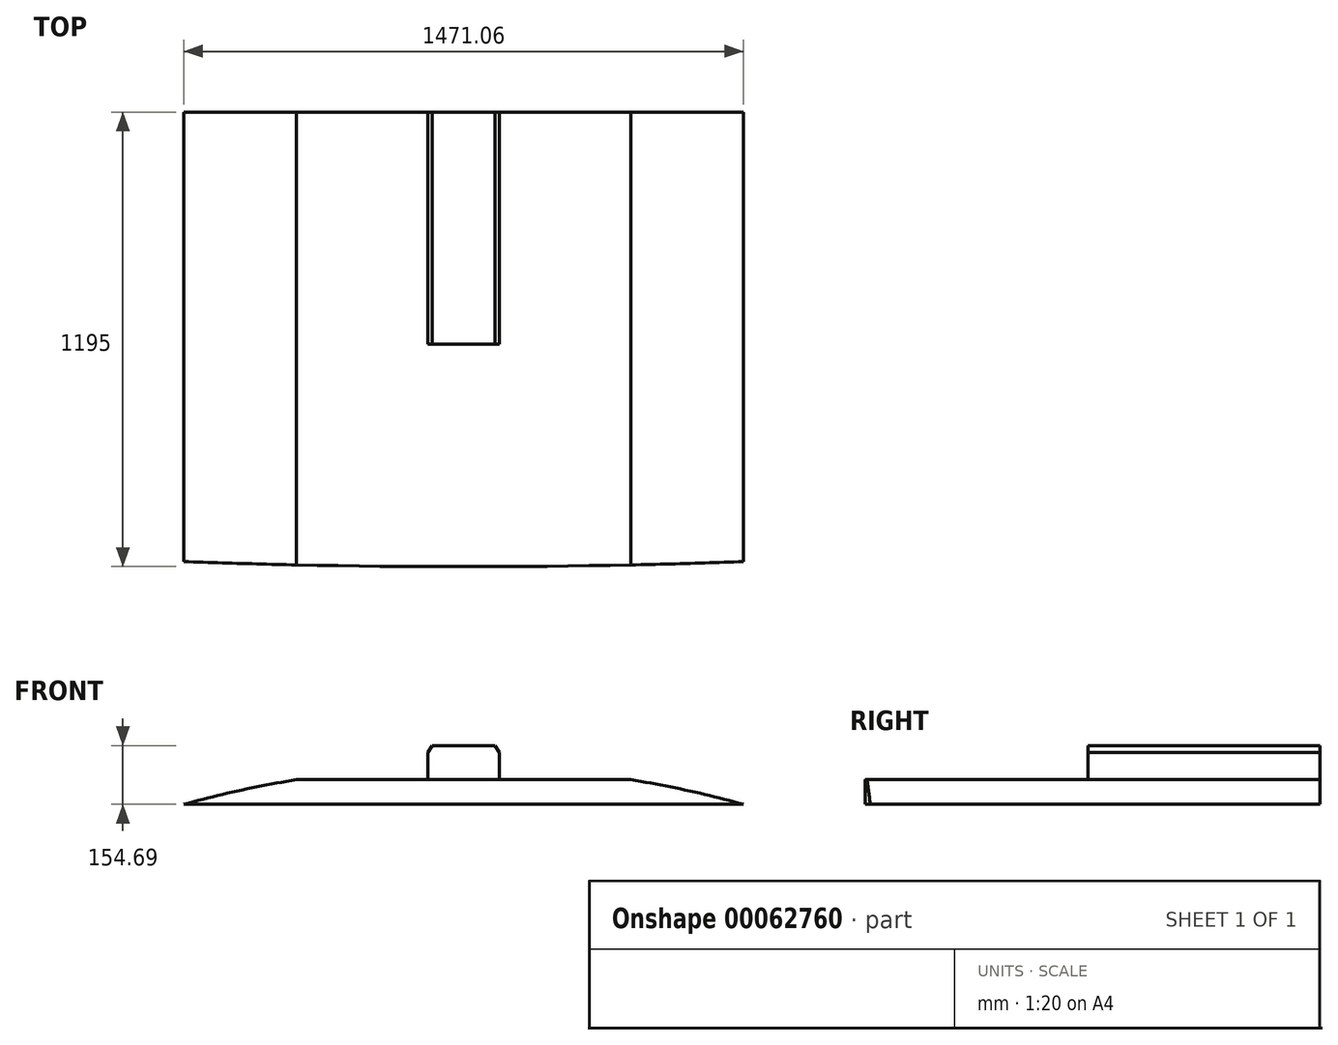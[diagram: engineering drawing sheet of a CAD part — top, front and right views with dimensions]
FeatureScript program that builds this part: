
annotation { "Feature Type Name" : "Feature", "Feature Type Description" : "" }
export const myFeature = defineFeature(function(context is Context, id is Id, definition is map)
    precondition{}
    {
        {
            var Q0;
            Q0=qCreatedBy(makeId("Front.planeOp"),FACE);
            var sketch = newSketch(context, id + "F0", { "sketchPlane" : qUnion([Q0])});
            skArc(sketch, "E0", {"start": v(1235.52, 2462.42) * mm, "mid": v(634.84, 2680.86) * mm, "end": v(0, 2755) * mm});
            skLineSegment(sketch, "E1", {"start": v(0, 0) * mm, "end": v(1355.2, 0) * mm, "construction": true});
            skLineSegment(sketch, "E2", {"start": v(1355.2, 0) * mm, "end": v(1355.2, 2268.47) * mm, "construction": true});
            skArc(sketch, "E3", {"start": v(1355.2, 2268.47) * mm, "mid": v(1322.87, 2382.42) * mm, "end": v(1235.52, 2462.42) * mm});
            skLineSegment(sketch, "E4", {"start": v(0, 0) * mm, "end": v(1407, 0) * mm, "construction": true});
            skLineSegment(sketch, "E5", {"start": v(1407, 0) * mm, "end": v(1407, 2368.62) * mm, "construction": true});
            skLineSegment(sketch, "E6", {"start": v(1355.2, 2268.47) * mm, "end": v(1357.8, 2155) * mm});
            skLineSegment(sketch, "E7", {"start": v(0, 2755) * mm, "end": v(0, 2155) * mm, "construction": true});
            skLineSegment(sketch, "E8", {"start": v(0, 2155) * mm, "end": v(1357.8, 2155) * mm});
            skArc(sketch, "E9.trimOffspring", {"start": v(1407, 2368.62) * mm, "mid": v(1381.18, 2383.77) * mm, "end": v(1355.2, 2398.64) * mm});
            skArc(sketch, "E10.MirrorCS", {"start": v(-1235.52, 2462.42) * mm, "mid": v(-634.84, 2680.86) * mm, "end": v(0, 2755) * mm});
            skArc(sketch, "E11.MirrorCS", {"start": v(-1355.2, 2268.47) * mm, "mid": v(-1322.87, 2382.42) * mm, "end": v(-1235.52, 2462.42) * mm});
            skLineSegment(sketch, "E12.MirrorCS", {"start": v(-1355.2, 2268.47) * mm, "end": v(-1357.8, 2155) * mm});
            skLineSegment(sketch, "E13.MirrorCS", {"start": v(0, 2155) * mm, "end": v(-1357.8, 2155) * mm});
            skSolve(sketch);
        }
        {
            var Q0;
            Q0=makeQuery(id+"F0.imprint","IMPRINT",FACE,{"disambiguationData":[TD([[makeQuery(id+"F0.imprint","IMPRINT",EDGE,{"derivedFrom":sQuery(id+"F0.wireOp",EDGE,"E0")}),1.0]])]});
            extrude(context, id + "F1", {"entities" : qUnion([Q0]), "oppositeDirection" : true, "depth" : 2000 * mm});
        }
        {
            var Q0;
            Q0=makeQuery(id+"F1.opExtrude","SWEPT_FACE",FACE,{"disambiguationData":[OSD([sQuery(id+"F0.wireOp",EDGE,"E8"),sQuery(id+"F0.wireOp",EDGE,"E13.MirrorCS")])]});
            var sketch = newSketch(context, id + "F2", { "sketchPlane" : qUnion([Q0])});
            skArc(sketch, "E14", {"start": v(1357.8, -50) * mm, "mid": v(0, -5) * mm, "end": v(-1357.8, -50) * mm});
            skLineSegment(sketch, "E15.0", {"start": v(1357.8, 0) * mm, "end": v(-1357.8, 0) * mm});
            skLineSegment(sketch, "E16", {"start": v(1357.8, -50) * mm, "end": v(1357.8, 0) * mm});
            skLineSegment(sketch, "E17", {"start": v(-1357.8, -50) * mm, "end": v(-1357.8, 0) * mm});
            skSolve(sketch);
        }
        {
            var Q0;
            Q0=qSketchRegion(id+"F2",true);
            extrude(context, id + "F3", {"entities" : qUnion([Q0]), "operationType" : NewBodyOperationType.REMOVE, "endBound" : BoundingType.THROUGH_ALL, "oppositeDirection" : true, "depth" : 25 * mm});
        }
        {
            var Q0;
            Q0=makeQuery(id+"F1.opExtrude","CAP_FACE",FACE,{"disambiguationData":[OSD([sQuery(id+"F0.wireOp",EDGE,"E0"),sQuery(id+"F0.wireOp",EDGE,"E3"),sQuery(id+"F0.wireOp",EDGE,"E6"),sQuery(id+"F0.wireOp",EDGE,"E8"),sQuery(id+"F0.wireOp",EDGE,"E10.MirrorCS"),sQuery(id+"F0.wireOp",EDGE,"E11.MirrorCS"),sQuery(id+"F0.wireOp",EDGE,"E12.MirrorCS"),sQuery(id+"F0.wireOp",EDGE,"E13.MirrorCS")])],"isStart":false});
            var sketch = newSketch(context, id + "F4", { "sketchPlane" : qUnion([Q0])});
            skPoint(sketch, "E18", {"position": v(0, 2755) * mm});
            skSolve(sketch);
        }
        {
            var Q0;
            Q0=makeQuery(id+"F4.imprint","IMPRINT",FACE,{"disambiguationData":[TD([[makeQuery(id+"F4.imprint","IMPRINT",EDGE,{"derivedFrom":makeQuery(id+"F1.opExtrude","CAP_EDGE",EDGE,{"disambiguationData":[OSD([sQuery(id+"F0.wireOp",EDGE,"E3")])],"isStart":false})}),-1.0]])]});
            var sketch = newSketch(context, id + "F5", { "sketchPlane" : qUnion([Q0])});
            skArc(sketch, "E19.0", {"start": v(-290, 2739.7) * mm, "mid": v(0, 2755) * mm, "end": v(290, 2739.7) * mm, "construction": true});
            skLineSegment(sketch, "E20", {"start": v(0, 2739.7) * mm, "end": v(290, 2739.7) * mm, "construction": true});
            skPoint(sketch, "E20.startSnap0", {"position": v(0, 2755) * mm});
            skLineSegment(sketch, "E21", {"start": v(0, 2739.7) * mm, "end": v(0, 2755) * mm, "construction": true});
            skLineSegment(sketch, "E22.MirrorCS", {"start": v(0, 2739.7) * mm, "end": v(-290, 2739.7) * mm, "construction": true});
            skPoint(sketch, "E23.orphan", {"position": v(1235.52, 2462.42) * mm});
            skPoint(sketch, "E24.orphan", {"position": v(-1235.52, 2462.42) * mm});
            skLineSegment(sketch, "E25", {"start": v(0, 2739.7) * mm, "end": v(0, 2719.7) * mm, "construction": true});
            skLineSegment(sketch, "E26", {"start": v(0, 2719.7) * mm, "end": v(439.65, 2719.7) * mm});
            skArc(sketch, "E27.0", {"start": v(0, 2755) * mm, "mid": v(634.84, 2680.86) * mm, "end": v(1235.52, 2462.42) * mm});
            skArc(sketch, "E28.MirrorCS", {"start": v(0, 2755) * mm, "mid": v(-634.84, 2680.86) * mm, "end": v(-1235.52, 2462.42) * mm});
            skLineSegment(sketch, "E29.MirrorCS", {"start": v(0, 2719.7) * mm, "end": v(-439.65, 2719.7) * mm});
            skSolve(sketch);
        }
        {
            var Q0;
            Q0=qSketchRegion(id+"F5",true);
            extrude(context, id + "F6", {"entities" : qUnion([Q0]), "operationType" : NewBodyOperationType.REMOVE, "endBound" : BoundingType.THROUGH_ALL, "oppositeDirection" : true, "depth" : 25 * mm});
        }
        {
            var Q0;
            Q0=makeQuery(id+"F4.imprint","IMPRINT",FACE,{"disambiguationData":[TD([[makeQuery(id+"F4.imprint","IMPRINT",EDGE,{"derivedFrom":makeQuery(id+"F1.opExtrude","CAP_EDGE",EDGE,{"disambiguationData":[OSD([sQuery(id+"F0.wireOp",EDGE,"E3")])],"isStart":false})}),-1.0]])]});
            var sketch = newSketch(context, id + "F7", { "sketchPlane" : qUnion([Q0])});
            skLineSegment(sketch, "E30.0", {"start": v(93.5, 2719.7) * mm, "end": v(-93.5, 2719.7) * mm});
            skLineSegment(sketch, "E31", {"start": v(0, 2719.7) * mm, "end": v(93.5, 2719.7) * mm, "construction": true});
            skLineSegment(sketch, "E32", {"start": v(93.5, 2719.7) * mm, "end": v(93.5, 2791.7) * mm});
            skLineSegment(sketch, "E33", {"start": v(93.5, 2791.7) * mm, "end": v(83.1, 2809.7) * mm});
            skLineSegment(sketch, "E34", {"start": v(83.1, 2809.7) * mm, "end": v(0, 2809.7) * mm});
            skLineSegment(sketch, "E35", {"start": v(0, 2809.7) * mm, "end": v(0, 2719.7) * mm, "construction": true});
            skLineSegment(sketch, "E36.MirrorCS", {"start": v(-83.1, 2809.7) * mm, "end": v(0, 2809.7) * mm});
            skLineSegment(sketch, "E37.MirrorCS", {"start": v(-93.5, 2791.7) * mm, "end": v(-83.1, 2809.7) * mm});
            skLineSegment(sketch, "E38.MirrorCS", {"start": v(-93.5, 2719.7) * mm, "end": v(-93.5, 2791.7) * mm});
            skSolve(sketch);
        }
        {
            var Q0;
            {var subQ5=sQuery(id+"F7.wireOp",EDGE,"E33");Q0=makeQuery(id+"F7.imprint","IMPRINT",FACE,{"disambiguationData":[TD([[makeQuery(id+"F7.imprint","IMPRINT",EDGE,{"derivedFrom":subQ5}),1.0]])]});}
            var Q1;
            {var subQ3=sQuery(id+"F7.wireOp",EDGE,"E30.0");Q1=makeQuery(id+"F7.imprint","IMPRINT",FACE,{"disambiguationData":[TD([[makeQuery(id+"F7.imprint","IMPRINT",EDGE,{"derivedFrom":subQ3}),-1.0]])]});}
            var Q2;
            {var subQ5=sQuery(id+"F7.wireOp",EDGE,"E31");Q2=makeQuery(id+"F7.imprint","IMPRINT",FACE,{"disambiguationData":[TD([[makeQuery(id+"F7.imprint","IMPRINT",EDGE,{"derivedFrom":subQ5}),1.0]])]});}
            var Q3;
            {var subQ3=sQuery(id+"F7.wireOp",EDGE,"E36.MirrorCS");Q3=makeQuery(id+"F7.imprint","IMPRINT",FACE,{"disambiguationData":[TD([[makeQuery(id+"F7.imprint","IMPRINT",EDGE,{"derivedFrom":subQ3}),-1.0]])]});}
            extrude(context, id + "F8", {"entities" : qUnion([Q0, Q1, Q2, Q3]), "operationType" : NewBodyOperationType.ADD, "oppositeDirection" : true, "depth" : (900 + 510) * mm});
        }
        {
            var Q0;
            Q0=makeQuery(id+"F4.imprint","IMPRINT",FACE,{"disambiguationData":[TD([[makeQuery(id+"F4.imprint","IMPRINT",EDGE,{"derivedFrom":makeQuery(id+"F1.opExtrude","CAP_EDGE",EDGE,{"disambiguationData":[OSD([sQuery(id+"F0.wireOp",EDGE,"E3")])],"isStart":false})}),-1.0]])]});
            var sketch = newSketch(context, id + "F9", { "sketchPlane" : qUnion([Q0])});
            skArc(sketch, "E39.0.0", {"start": v(1235.52, 2462.42) * mm, "mid": v(847.4, 2621.44) * mm, "end": v(439.65, 2719.7) * mm});
            skLineSegment(sketch, "E39.0.1", {"start": v(439.65, 2719.7) * mm, "end": v(93.5, 2719.7) * mm});
            skLineSegment(sketch, "E39.0.2", {"start": v(93.5, 2719.7) * mm, "end": v(93.5, 2791.7) * mm});
            skLineSegment(sketch, "E39.0.3", {"start": v(93.5, 2791.7) * mm, "end": v(83.1, 2809.7) * mm});
            skLineSegment(sketch, "E39.0.4", {"start": v(83.1, 2809.7) * mm, "end": v(-83.1, 2809.7) * mm});
            skLineSegment(sketch, "E39.0.5", {"start": v(-83.1, 2809.7) * mm, "end": v(-93.5, 2791.7) * mm});
            skLineSegment(sketch, "E39.0.6", {"start": v(-93.5, 2791.7) * mm, "end": v(-93.5, 2719.7) * mm});
            skLineSegment(sketch, "E39.0.7", {"start": v(-93.5, 2719.7) * mm, "end": v(-439.65, 2719.7) * mm});
            skArc(sketch, "E39.0.8", {"start": v(-439.65, 2719.7) * mm, "mid": v(-847.4, 2621.44) * mm, "end": v(-1235.52, 2462.42) * mm});
            skArc(sketch, "E39.0.9", {"start": v(-1235.52, 2462.42) * mm, "mid": v(-1322.87, 2382.42) * mm, "end": v(-1355.2, 2268.47) * mm});
            skLineSegment(sketch, "E39.0.10", {"start": v(-1355.2, 2268.47) * mm, "end": v(-1357.8, 2155) * mm});
            skLineSegment(sketch, "E39.0.11", {"start": v(-1357.8, 2155) * mm, "end": v(1357.8, 2155) * mm});
            skLineSegment(sketch, "E39.0.12", {"start": v(1357.8, 2155) * mm, "end": v(1355.2, 2268.47) * mm});
            skArc(sketch, "E39.0.13", {"start": v(1355.2, 2268.47) * mm, "mid": v(1322.87, 2382.42) * mm, "end": v(1235.52, 2462.42) * mm});
            skSolve(sketch);
        }
        {
            var Q0;
            Q0=qSketchRegion(id+"F9",true);
            extrude(context, id + "F10", {"entities" : qUnion([Q0]), "operationType" : NewBodyOperationType.REMOVE, "oppositeDirection" : true, "depth" : 800 * mm});
        }
        {
            var Q0;
            Q0=makeQuery(id+"F4.imprint","IMPRINT",FACE,{"disambiguationData":[TD([[makeQuery(id+"F4.imprint","IMPRINT",EDGE,{"derivedFrom":makeQuery(id+"F1.opExtrude","CAP_EDGE",EDGE,{"disambiguationData":[OSD([sQuery(id+"F0.wireOp",EDGE,"E3")])],"isStart":false})}),-1.0]])]});
            var sketch = newSketch(context, id + "F11", { "sketchPlane" : qUnion([Q0])});
            skArc(sketch, "E40.0.2", {"start": v(-735.53, 2655) * mm, "mid": v(-990.21, 2570.9) * mm, "end": v(-1235.52, 2462.42) * mm});
            skArc(sketch, "E40.0.3", {"start": v(-1235.52, 2462.42) * mm, "mid": v(-1322.87, 2382.42) * mm, "end": v(-1355.2, 2268.47) * mm});
            skLineSegment(sketch, "E40.0.4", {"start": v(-1355.2, 2268.47) * mm, "end": v(-1357.8, 2155) * mm});
            skLineSegment(sketch, "E40.0.5", {"start": v(-1357.8, 2155) * mm, "end": v(1357.8, 2155) * mm});
            skLineSegment(sketch, "E40.0.6", {"start": v(1357.8, 2155) * mm, "end": v(1355.2, 2268.47) * mm});
            skArc(sketch, "E40.0.7", {"start": v(1355.2, 2268.47) * mm, "mid": v(1322.87, 2382.42) * mm, "end": v(1235.52, 2462.42) * mm});
            skArc(sketch, "E40.0.8", {"start": v(1235.52, 2462.42) * mm, "mid": v(990.21, 2570.9) * mm, "end": v(735.53, 2655) * mm});
            skLineSegment(sketch, "E41", {"start": v(-735.53, 2655) * mm, "end": v(735.53, 2655) * mm});
            skSolve(sketch);
        }
        {
            var Q0;
            Q0=makeQuery(id+"F11.imprint","IMPRINT",FACE,{"disambiguationData":[TD([[makeQuery(id+"F11.imprint","IMPRINT",EDGE,{"derivedFrom":sQuery(id+"F11.wireOp",EDGE,"E40.0.2")}),-1.0]])]});
            extrude(context, id + "F12", {"entities" : qUnion([Q0]), "operationType" : NewBodyOperationType.REMOVE, "endBound" : BoundingType.THROUGH_ALL, "oppositeDirection" : true, "depth" : 25 * mm});
        }
    });
